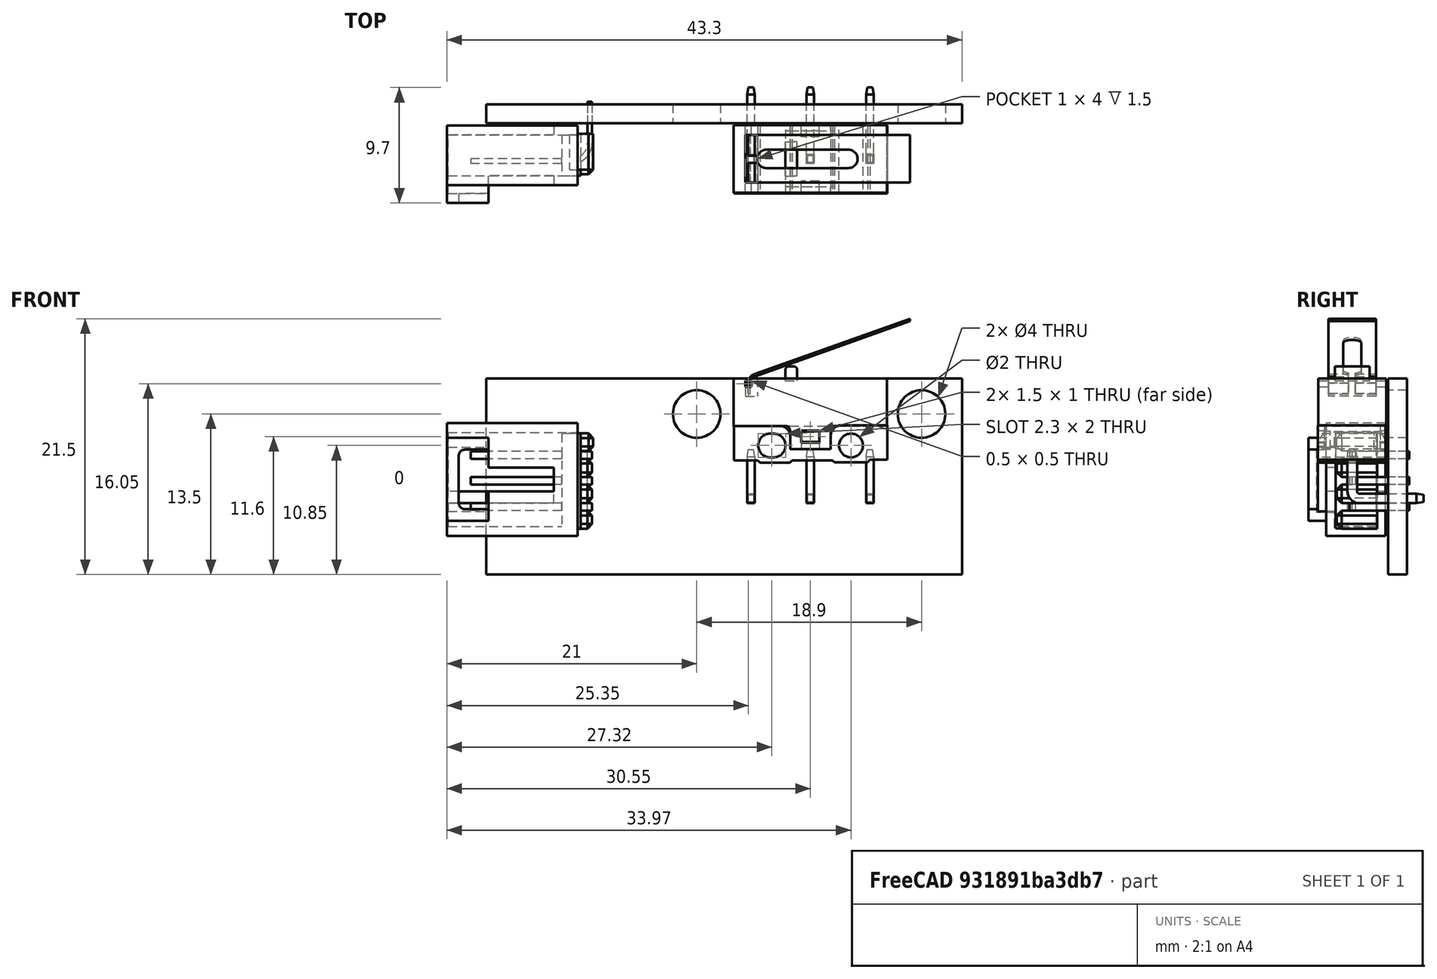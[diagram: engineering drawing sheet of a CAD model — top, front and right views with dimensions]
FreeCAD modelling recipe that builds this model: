
FCSTD DOCUMENT  (FreeCAD 0.14R3692 (Git))
Label: sensorEndStop
License: CC-BY 3.0
LicenseURL: http://creativecommons.org/licenses/by/3.0/
objects: Part::Cut×4, Part::MultiFuse×3, Part::Cylinder×2, Part::Fillet×2, Part::Box×1, Part::FeaturePython×1, App::DocumentObjectGroup×1
note: 13 computed .brp shape members not serialized (recipe doc carries the construction recipe); baked Part::Feature solids carry a one-line shape summary decoded from their .brp

FEATURE [Part::Box] Box  label="prePlaca"
  Height = 16.5
  Length = 40
  Width = 1.6
FEATURE [Part::Cylinder] Cylinder  label="Cilindro"
  Angle = 360
  Height = 10
  Placement = pos=(17.7,8,13.5) rot=(1,0,0;1.5708rad)
  Radius = 2
FEATURE [Part::Cylinder] Cylinder001  label="Cilindro001"
  Angle = 360
  Height = 10
  Placement = pos=(36.6,8,13.5) rot=(1,0,0;1.5708rad)
  Radius = 2
FEATURE [Part::Cut] Cut001
  Base = -> Box
  Tool = -> Cylinder
FEATURE [Part::Cut] Cut002  label="Placa"
  Base = -> Cut001
  Tool = -> Cylinder001
FEATURE [Part::Fillet] Fillet  label="Cuerpo"
  Edges = 4 edges r=0.4: [Edge27,Edge29,Edge33,Edge35]
  Placement = pos=(27.25,-3,12.5) rot=(0,0,1;0rad)
FEATURE [Part::MultiFuse] Fusion  label="base"
  Placement = pos=(27.25,-3,12.5) rot=(0,0,1;0rad)
FEATURE [Part::Cut] Cut  label="Palanca"
  Placement = pos=(27.25,-3,12.5) rot=(0,0,1;0rad)
FEATURE [Part::FeaturePython] Array  label="Pines"  # Draft array (typed FeaturePython)
  Angle = 360
  ArrayType = 0
  Axis = (0,0,1)
  Center = (0,0,0)
  IntervalX = (5,0,0)
  IntervalY = (0,1,0)
  IntervalZ = (0,0,1)
  NumberPolar = 1
  NumberX = 3
  NumberY = 1
  NumberZ = 1
  Placement = pos=(22.25,-3,12.5) rot=(0,0,1;0rad)
FEATURE [Part::Fillet] Fillet001  label="pulsador"
  Edges = 2 edges r=0.3: [Edge2,Edge6]
  Placement = pos=(27.25,-3,12.5) rot=(0,0,1;0rad)
FEATURE [App::DocumentObjectGroup] Grupo  label="GR_EndStop"
  Group = -> [Fillet,Fusion,Cut,Array,Fillet001]
FEATURE [Part::MultiFuse] Fusion002  label="Conectores"
  Placement = pos=(0,0.7,0.7) rot=(0,0,1;1.5708rad)
FEATURE [Part::Cut] Cut003  label="AlojaConectores"
  Placement = pos=(0,0.7,0.7) rot=(0,0,1;1.5708rad)
FEATURE [Part::MultiFuse] Fusion001  label="Conector3pin"
  Placement = pos=(15,1.5,8) rot=(0.57735,0.57735,-0.57735;2.0944rad)
  Shapes = -> [Fusion002,Cut003]
